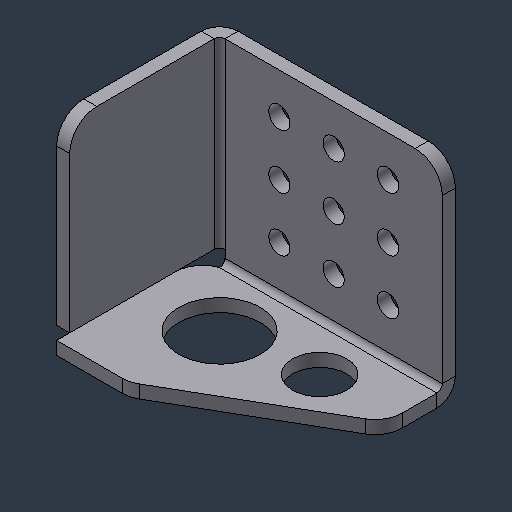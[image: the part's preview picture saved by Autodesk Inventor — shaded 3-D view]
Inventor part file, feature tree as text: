
AUTODESK INVENTOR PART (.ipt)
format: ipt  version: 2024.3 (Build 283343000, 343)  size: 342,016 bytes
history: native  units: mm (DEFAULTED — no unit token found)
features: sheet_metal_op x8, sketch x6, other x5, hole x3, pattern_linear x1, chamfer x1
ambient origin geometry x8: Origin, YZ Plane, XZ Plane, XY Plane, X Axis, Y Axis, Z Axis, Center Point
bodies: Solid1 (feature_tree)
feature tree (24):
  sheet_metal_op  "Face1"
  hole  "Hole1"  [1 undecoded]
  pattern_linear  "Rectangular Pattern1"  Count1=3 Spacing1=12.7mm
  sheet_metal_op  "Flange1"
  sheet_metal_op  "Flange2"
  other  "Corner Chamfer1"
  hole  "Hole2"  [1 undecoded]
  hole  "Hole3"  [1 undecoded]
  chamfer  "Corner Round1"
  sketch  "Sketch1"  dims[d0=50.8mm d1=44.45mm]
  other  "Plate1"
  sketch  "Sketch2"  dims[d2=3.048mm]
  sketch  "Sketch3"  dims[d3=4.9784mm d4=19.05mm d5=9.779mm d6=1.9558mm d7=14.3117mm d8=3.048mm]
  other  "Plate2"
  sheet_metal_op  "Bend1"
  sheet_metal_op  "Corner1"
  sketch  "Sketch4"  dims[d9=20.594885mm d10=30.0mm d12=12.7mm]
  other  "Plate3"
  sheet_metal_op  "Bend2"
  sheet_metal_op  "Corner2"
  sketch  "Sketch5"  dims[d13=3.048mm d14=1.524mm]
  sketch  "Sketch6"  dims[d15=6.096mm d16=4.572mm d17=38.1mm d18=90.0deg d19=1.27mm d20=12.192mm d21=3.048mm d22=4.572mm d23=30.0mm d25=12.7mm d26=6.35mm d27=3.048mm d28=1.524mm d29=6.096mm d30=4.572mm d31=38.1mm d32=90.0deg d33=1.27mm d34=12.192mm d35=3.048mm d36=4.572mm d37=12.192mm d38=4.572mm d39=3.048mm d40=0.0mm d41=10.0mm d42=38.1mm d43=6.35mm d44=30.0deg d45=19.05mm d46=19.05mm d47=9.525mm d48=6.35mm d49=14.3117mm d50=3.048mm d51=20.594885mm d52=12.7mm d53=19.05mm d54=9.525mm d55=6.35mm d56=14.3117mm d57=3.048mm d58=20.594885mm]
  sheet_metal_op  "Corner3"
  other  "Definition1"
note: 3 required parameter values undecoded (feature->parameter linkage not recoverable at this tier; creation-order binding heuristic only, values carry confidence <= 0.55)
